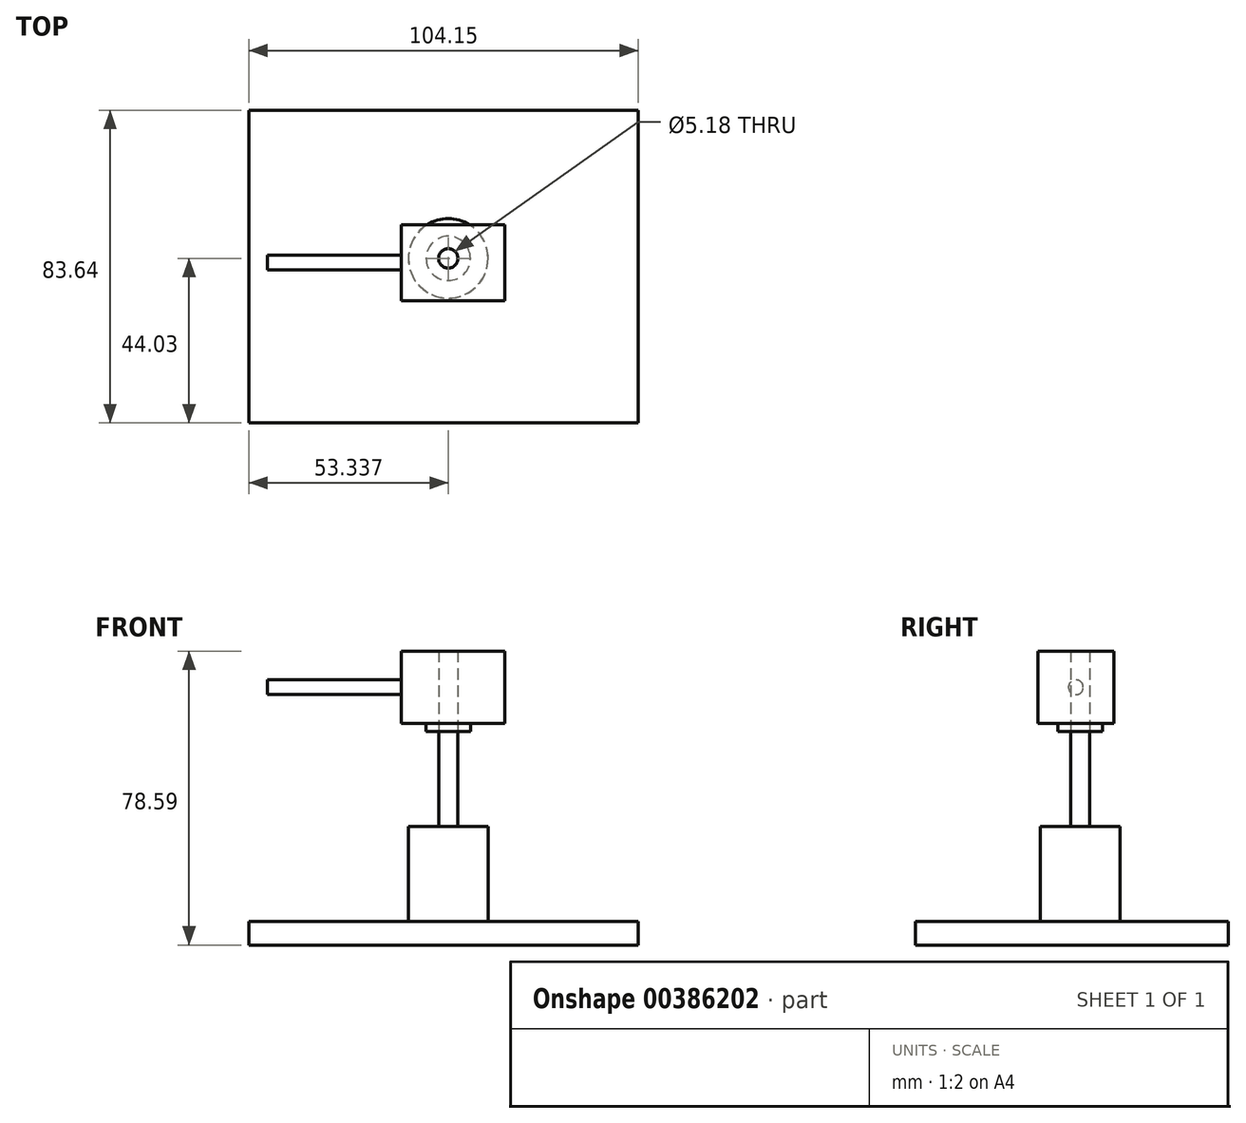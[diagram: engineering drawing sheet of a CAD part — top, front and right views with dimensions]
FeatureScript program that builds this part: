
annotation { "Feature Type Name" : "Feature", "Feature Type Description" : "" }
export const myFeature = defineFeature(function(context is Context, id is Id, definition is map)
    precondition{}
    {
        {
            var Q0;
            Q0=qCreatedBy(makeId("Top.planeOp"),FACE);
            var sketch = newSketch(context, id + "F0", { "sketchPlane" : qUnion([Q0])});
            skLineSegment(sketch, "E0.bottom", {"start": v(-47.34, 39.61) * mm, "end": v(56.81, 39.61) * mm});
            skLineSegment(sketch, "E0.top", {"start": v(-47.34, -44.03) * mm, "end": v(56.81, -44.03) * mm});
            skLineSegment(sketch, "E0.left", {"start": v(-47.34, 39.61) * mm, "end": v(-47.34, -44.03) * mm});
            skLineSegment(sketch, "E0.right", {"start": v(56.81, 39.61) * mm, "end": v(56.81, -44.03) * mm});
            skSolve(sketch);
        }
        {
            var Q0;
            Q0=makeQuery(id+"F0.imprint","IMPRINT",FACE,{"disambiguationData":[TD([[makeQuery(id+"F0.imprint","IMPRINT",EDGE,{"derivedFrom":sQuery(id+"F0.wireOp",EDGE,"E0.bottom")}),-1.0]])]});
            extrude(context, id + "F1", {"entities" : qUnion([Q0]), "depth" : 6.35 * mm});
        }
        {
            var Q0;
            Q0=makeQuery(id+"F1.opExtrude","CAP_FACE",FACE,{"disambiguationData":[OSD([sQuery(id+"F0.wireOp",EDGE,"E0.bottom"),sQuery(id+"F0.wireOp",EDGE,"E0.top"),sQuery(id+"F0.wireOp",EDGE,"E0.left"),sQuery(id+"F0.wireOp",EDGE,"E0.right")])],"isStart":false});
            var sketch = newSketch(context, id + "F2", { "sketchPlane" : qUnion([Q0])});
            skCircle(sketch, "E1", {"center": v(6, 0) * mm, "radius": 10.65 * mm});
            skSolve(sketch);
        }
        {
            var Q0;
            Q0=makeQuery(id+"F2.imprint","IMPRINT",FACE,{"disambiguationData":[TD([[makeQuery(id+"F2.imprint","IMPRINT",EDGE,{"derivedFrom":sQuery(id+"F2.wireOp",EDGE,"E1")}),1.0]])]});
            extrude(context, id + "F3", {"entities" : qUnion([Q0]), "operationType" : NewBodyOperationType.ADD, "depth" : 25.4 * mm});
        }
        {
            var Q0;
            Q0=makeQuery(id+"F3.opExtrude","CAP_FACE",FACE,{"disambiguationData":[OSD([sQuery(id+"F2.wireOp",EDGE,"E1")])],"isStart":false});
            var sketch = newSketch(context, id + "F4", { "sketchPlane" : qUnion([Q0])});
            skCircle(sketch, "E2", {"center": v(6, 0) * mm, "radius": 2.59 * mm});
            skSolve(sketch);
        }
        {
            var Q0;
            Q0=makeQuery(id+"F4.imprint","IMPRINT",FACE,{"disambiguationData":[TD([[makeQuery(id+"F4.imprint","IMPRINT",EDGE,{"derivedFrom":sQuery(id+"F4.wireOp",EDGE,"E2")}),1.0]])]});
            var sketch = newSketch(context, id + "F5", { "sketchPlane" : qUnion([Q0])});
            skSolve(sketch);
        }
        {
            var Q0;
            Q0=makeQuery(id+"F5.imprint","IMPRINT",FACE,{"disambiguationData":[TD([[makeQuery(id+"F5.imprint","IMPRINT",EDGE,{"derivedFrom":makeQuery(id+"F4.imprint","IMPRINT",EDGE,{"derivedFrom":sQuery(id+"F4.wireOp",EDGE,"E2")})}),1.0]])]});
            extrude(context, id + "F6", {"entities" : qUnion([Q0]), "operationType" : NewBodyOperationType.ADD, "depth" : 25.4 * mm});
        }
        {
            var Q0;
            Q0=makeQuery(id+"F6.opExtrude","CAP_FACE",FACE,{"disambiguationData":[OSD([sQuery(id+"F4.wireOp",EDGE,"E2")])],"isStart":false});
            var sketch = newSketch(context, id + "F7", { "sketchPlane" : qUnion([Q0])});
            skCircle(sketch, "E3", {"center": v(6, 0) * mm, "radius": 5.92 * mm});
            skSolve(sketch);
        }
        {
            var Q0;
            Q0=makeQuery(id+"F7.imprint","IMPRINT",FACE,{"disambiguationData":[TD([[makeQuery(id+"F7.imprint","IMPRINT",EDGE,{"derivedFrom":sQuery(id+"F7.wireOp",EDGE,"E3")}),1.0]])]});
            extrude(context, id + "F8", {"entities" : qUnion([Q0]), "depth" : 2.13 * mm});
        }
        {
            var Q0;
            Q0=makeQuery(id+"F8.opExtrude","CAP_FACE",FACE,{"disambiguationData":[OSD([sQuery(id+"F4.wireOp",EDGE,"E2"),sQuery(id+"F7.wireOp",EDGE,"E3")])],"isStart":false});
            var sketch = newSketch(context, id + "F9", { "sketchPlane" : qUnion([Q0])});
            skLineSegment(sketch, "E4.bottom", {"start": v(-6.52, 9.04) * mm, "end": v(21.1, 9.04) * mm});
            skLineSegment(sketch, "E4.top", {"start": v(-6.52, -11.33) * mm, "end": v(21.1, -11.33) * mm});
            skLineSegment(sketch, "E4.left", {"start": v(-6.52, 9.04) * mm, "end": v(-6.52, -11.33) * mm});
            skLineSegment(sketch, "E4.right", {"start": v(21.1, 9.04) * mm, "end": v(21.1, -11.33) * mm});
            skSolve(sketch);
        }
        {
            var Q0;
            Q0=makeQuery(id+"F9.imprint","IMPRINT",FACE,{"disambiguationData":[TD([[makeQuery(id+"F9.imprint","IMPRINT",EDGE,{"derivedFrom":sQuery(id+"F9.wireOp",EDGE,"E4.bottom")}),-1.0]])]});
            var Q1;
            Q1=makeQuery(id+"F9.imprint","IMPRINT",FACE,{"disambiguationData":[TD([[makeQuery(id+"F9.imprint","IMPRINT",EDGE,{"derivedFrom":makeQuery(id+"F8.opExtrude","CAP_EDGE",EDGE,{"disambiguationData":[OSD([sQuery(id+"F7.wireOp",EDGE,"E3")])],"isStart":false})}),1.0]])]});
            extrude(context, id + "F10", {"entities" : qUnion([Q0, Q1]), "operationType" : NewBodyOperationType.ADD, "depth" : 19.3 * mm});
        }
        {
            var Q0;
            Q0=makeQuery(id+"F10.opExtrude","SWEPT_FACE",FACE,{"disambiguationData":[OSD([sQuery(id+"F9.wireOp",EDGE,"E4.left")])]});
            var sketch = newSketch(context, id + "F11", { "sketchPlane" : qUnion([Q0])});
            skCircle(sketch, "E5", {"center": v(1.15, 68.94) * mm, "radius": 1.98 * mm});
            skPoint(sketch, "E5.centerSnap0", {"position": v(11.33, 68.94) * mm});
            skPoint(sketch, "E5.centerSnap1", {"position": v(1.15, 59.28) * mm});
            skSolve(sketch);
        }
        {
            var Q0;
            Q0 = qSketchRegion(id + "F11", true);
            extrude(context, id + "F12", {"entities" : qUnion([Q0]), "operationType" : NewBodyOperationType.ADD, "depth" : 35.81 * mm});
        }
    });
